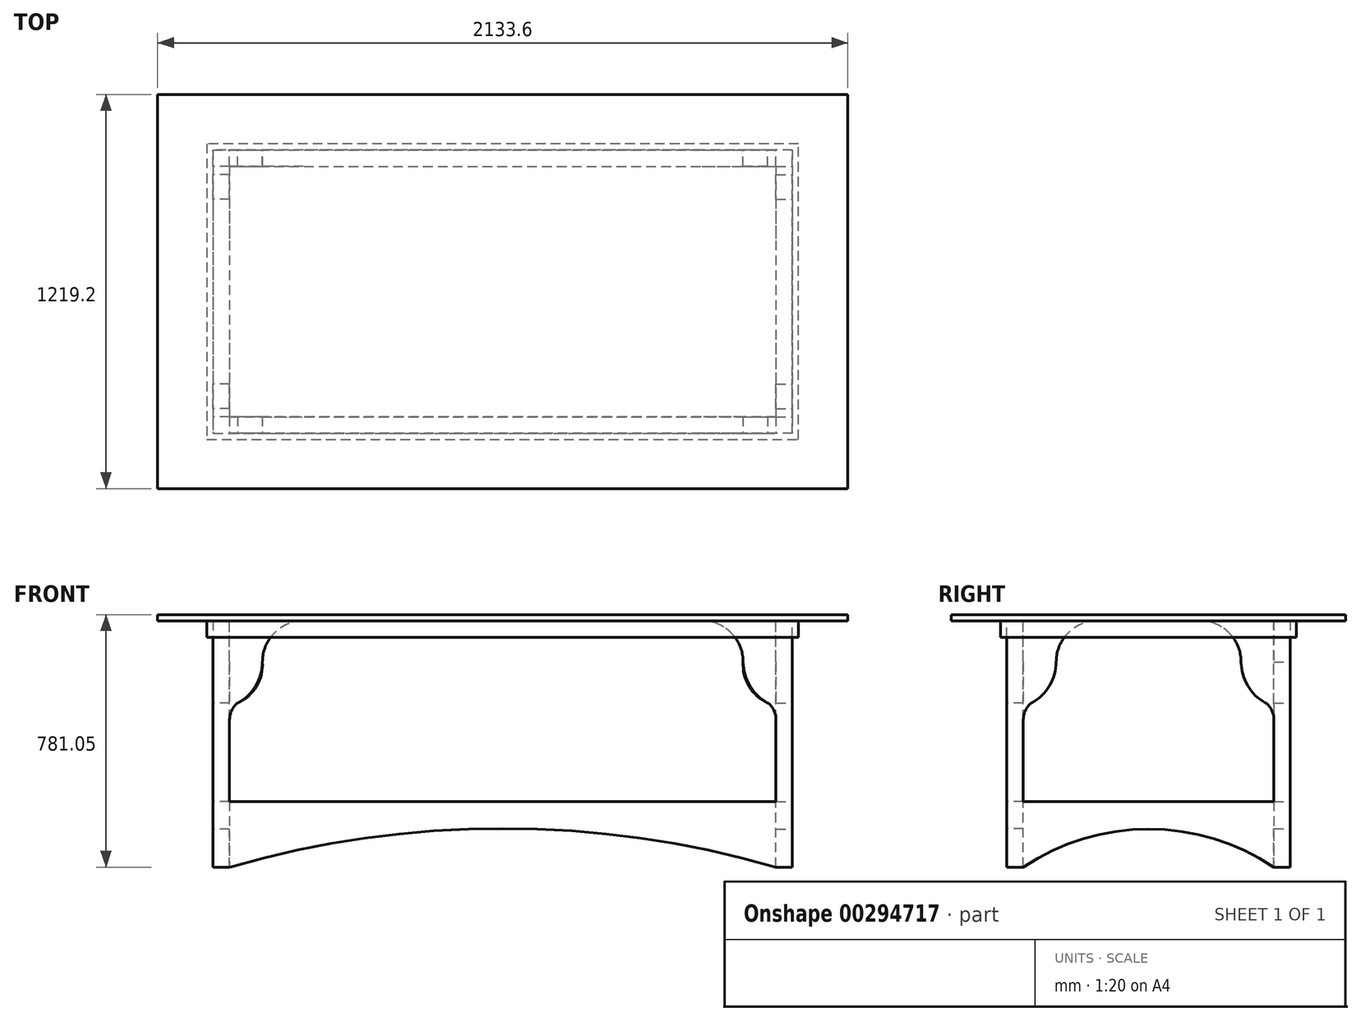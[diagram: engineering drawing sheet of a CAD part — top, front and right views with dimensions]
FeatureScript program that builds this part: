
annotation { "Feature Type Name" : "Feature", "Feature Type Description" : "" }
export const myFeature = defineFeature(function(context is Context, id is Id, definition is map)
    precondition{}
    {
        {
            var Q0;
            Q0=qCreatedBy(makeId("Top.planeOp"),FACE);
            var sketch = newSketch(context, id + "F0", { "sketchPlane" : qUnion([Q0])});
            skLineSegment(sketch, "E0", {"start": v(0, 609.6) * mm, "end": v(-1066.8, 609.6) * mm});
            skLineSegment(sketch, "E1", {"start": v(-1066.8, 609.6) * mm, "end": v(1066.8, 609.6) * mm});
            skLineSegment(sketch, "E2", {"start": v(1066.8, 609.6) * mm, "end": v(1066.8, -609.6) * mm});
            skLineSegment(sketch, "E3", {"start": v(1066.8, -609.6) * mm, "end": v(-1066.8, -609.6) * mm});
            skLineSegment(sketch, "E4", {"start": v(-1066.8, -609.6) * mm, "end": v(-1066.8, 609.6) * mm});
            skLineSegment(sketch, "E5", {"start": v(-1066.8, -609.6) * mm, "end": v(-1028.7, -609.6) * mm});
            skLineSegment(sketch, "E6", {"start": v(-1028.7, -571.5) * mm, "end": v(-1028.7, 571.5) * mm});
            skLineSegment(sketch, "E7", {"start": v(-1028.7, 571.5) * mm, "end": v(1028.7, 571.5) * mm});
            skLineSegment(sketch, "E8", {"start": v(1028.7, 571.5) * mm, "end": v(1028.7, -571.5) * mm});
            skLineSegment(sketch, "E9", {"start": v(1028.7, -571.5) * mm, "end": v(-1028.7, -571.5) * mm});
            skSolve(sketch);
        }
        {
            var Q0;
            Q0 = qSketchRegion(id + "F0", true);
            var Q1;
            Q1=makeQuery(id+"F0.imprint","IMPRINT",FACE,{"disambiguationData":[TD([[makeQuery(id+"F0.imprint","IMPRINT",EDGE,{"derivedFrom":sQuery(id+"F0.wireOp",EDGE,"E6")}),-1.0]])]});
            extrude(context, id + "F1", {"entities" : qUnion([Q0, Q1]), "depth" : 19.05 * mm});
        }
        {
            var Q0;
            Q0=makeQuery(id+"F1.opExtrude","CAP_FACE",FACE,{"disambiguationData":[OSD([sQuery(id+"F0.wireOp",EDGE,"E1"),sQuery(id+"F0.wireOp",EDGE,"E2"),sQuery(id+"F0.wireOp",EDGE,"E3"),sQuery(id+"F0.wireOp",EDGE,"E4"),sQuery(id+"F0.wireOp",EDGE,"E5")])],"isStart":true});
            var sketch = newSketch(context, id + "F2", { "sketchPlane" : qUnion([Q0])});
            skLineSegment(sketch, "E10", {"start": v(0, 0) * mm, "end": v(0, -457.2) * mm});
            skPoint(sketch, "E10.endSnap0", {"position": v(0, 609.6) * mm});
            skLineSegment(sketch, "E11", {"start": v(0, -457.2) * mm, "end": v(-914.4, -457.2) * mm});
            skLineSegment(sketch, "E12", {"start": v(-914.4, -457.2) * mm, "end": v(-914.4, 457.2) * mm});
            skLineSegment(sketch, "E13", {"start": v(-914.4, 457.2) * mm, "end": v(0, 457.2) * mm});
            skLineSegment(sketch, "E14", {"start": v(0, 457.2) * mm, "end": v(914.4, 457.2) * mm});
            skLineSegment(sketch, "E15", {"start": v(914.4, 457.2) * mm, "end": v(914.4, -457.2) * mm});
            skLineSegment(sketch, "E16", {"start": v(914.4, -457.2) * mm, "end": v(0, -457.2) * mm});
            skLineSegment(sketch, "E17.0", {"start": v(-895.35, -438.15) * mm, "end": v(-895.35, 438.15) * mm});
            skLineSegment(sketch, "E17.1", {"start": v(0, 438.15) * mm, "end": v(895.35, 438.15) * mm});
            skLineSegment(sketch, "E17.2", {"start": v(895.35, 438.15) * mm, "end": v(895.35, -438.15) * mm});
            skLineSegment(sketch, "E17.3", {"start": v(-895.35, 438.15) * mm, "end": v(0, 438.15) * mm});
            skLineSegment(sketch, "E17.4", {"start": v(895.35, -438.15) * mm, "end": v(0, -438.15) * mm});
            skLineSegment(sketch, "E17.5", {"start": v(0, -438.15) * mm, "end": v(-895.35, -438.15) * mm});
            skSolve(sketch);
        }
        {
            var Q0;
            Q0 = qSketchRegion(id + "F2", true);
            extrude(context, id + "F3", {"entities" : qUnion([Q0]), "operationType" : NewBodyOperationType.ADD, "depth" : 50.8 * mm});
        }
        {
            var Q0;
            Q0=makeQuery(id+"F3.opExtrude","SWEPT_FACE",FACE,{"disambiguationData":[OSD([sQuery(id+"F2.wireOp",EDGE,"E17.1"),sQuery(id+"F2.wireOp",EDGE,"E17.3")])]});
            var sketch = newSketch(context, id + "F4", { "sketchPlane" : qUnion([Q0])});
            skLineSegment(sketch, "E18", {"start": v(895.35, 0) * mm, "end": v(578.35, 0) * mm});
            skLineSegment(sketch, "E19", {"start": v(895.35, 0) * mm, "end": v(742.95, 0) * mm});
            skLineSegment(sketch, "E20", {"start": v(895.35, 0) * mm, "end": v(895.35, -762) * mm});
            skArc(sketch, "E21", {"start": v(742.95, -127) * mm, "mid": v(763.46, -201.05) * mm, "end": v(819.15, -254) * mm});
            skLineSegment(sketch, "E22", {"start": v(895.35, -762) * mm, "end": v(844.55, -762) * mm});
            skLineSegment(sketch, "E23", {"start": v(844.55, -762) * mm, "end": v(844.55, -304.8) * mm});
            skArc(sketch, "E24", {"start": v(844.55, -304.8) * mm, "mid": v(837.85, -276.4) * mm, "end": v(819.15, -254) * mm});
            skLineSegment(sketch, "E25", {"start": v(742.95, 0) * mm, "end": v(615.95, 0) * mm});
            skArc(sketch, "E26", {"start": v(742.95, -127) * mm, "mid": v(705.75, -37.2) * mm, "end": v(615.95, 0) * mm});
            skSolve(sketch);
        }
        {
            var Q0;
            Q0 = qSketchRegion(id + "F4", true);
            extrude(context, id + "F5", {"entities" : qUnion([Q0]), "operationType" : NewBodyOperationType.ADD, "depth" : 50.8 * mm});
        }
        {
            var Q0;
            Q0=makeQuery(id+"F3.opExtrude","SWEPT_FACE",FACE,{"disambiguationData":[OSD([sQuery(id+"F2.wireOp",EDGE,"E17.4"),sQuery(id+"F2.wireOp",EDGE,"E17.5")])]});
            var sketch = newSketch(context, id + "F6", { "sketchPlane" : qUnion([Q0])});
            skLineSegment(sketch, "E27", {"start": v(-895.35, 0) * mm, "end": v(-895.35, -762) * mm});
            skLineSegment(sketch, "E28", {"start": v(-895.35, -762) * mm, "end": v(-844.55, -762) * mm});
            skLineSegment(sketch, "E29", {"start": v(-844.55, -762) * mm, "end": v(-844.55, -304.8) * mm});
            skLineSegment(sketch, "E30", {"start": v(-895.35, 0) * mm, "end": v(-615.95, 0) * mm});
            skLineSegment(sketch, "E31", {"start": v(-615.95, 0) * mm, "end": v(-742.95, 0) * mm});
            skArc(sketch, "E32", {"start": v(-615.95, 0) * mm, "mid": v(-705.75, -37.2) * mm, "end": v(-742.95, -127) * mm});
            skLineSegment(sketch, "E33", {"start": v(-895.35, -127) * mm, "end": v(-895.35, -203.2) * mm});
            skArc(sketch, "E34", {"start": v(-819.15, -254) * mm, "mid": v(-760.9, -202.6) * mm, "end": v(-742.95, -127) * mm});
            skArc(sketch, "E35", {"start": v(-819.15, -254) * mm, "mid": v(-837.85, -276.4) * mm, "end": v(-844.55, -304.8) * mm});
            skSolve(sketch);
        }
        {
            var Q0;
            Q0 = qSketchRegion(id + "F6", true);
            extrude(context, id + "F7", {"entities" : qUnion([Q0]), "operationType" : NewBodyOperationType.ADD, "depth" : 50.8 * mm});
        }
        {
            var Q0;
            Q0=makeQuery(id+"F1.opExtrude","SWEPT_BODY",BODY,{"disambiguationData":[OSD([sQuery(id+"F0.wireOp",EDGE,"E1"),sQuery(id+"F0.wireOp",EDGE,"E2"),sQuery(id+"F0.wireOp",EDGE,"E3"),sQuery(id+"F0.wireOp",EDGE,"E4"),sQuery(id+"F0.wireOp",EDGE,"E5")])]});
            var Q1;
            Q1=qCreatedBy(makeId("Right.planeOp"),FACE);
            mirror(context, id + "F8", {"operationType" : NewBodyOperationType.ADD, "entities" : qUnion([Q0]), "mirrorPlane" : qUnion([Q1])});
        }
        {
            var Q0;
            Q0=makeQuery(id+"F8.opPattern","COPY",FACE,{"derivedFrom":makeQuery(id+"F5.opExtrude","CAP_FACE",FACE,{"disambiguationData":[OSD([sQuery(id+"F4.wireOp",EDGE,"E19"),sQuery(id+"F4.wireOp",EDGE,"E20"),sQuery(id+"F4.wireOp",EDGE,"E21"),sQuery(id+"F4.wireOp",EDGE,"E22"),sQuery(id+"F4.wireOp",EDGE,"E23"),sQuery(id+"F4.wireOp",EDGE,"E24"),sQuery(id+"F4.wireOp",EDGE,"E25"),sQuery(id+"F4.wireOp",EDGE,"E26")])],"isStart":true}),"instanceName":"1"});
            var sketch = newSketch(context, id + "F9", { "sketchPlane" : qUnion([Q0])});
            skLineSegment(sketch, "E36", {"start": v(-844.55, -762) * mm, "end": v(-844.55, -558.8) * mm});
            skLineSegment(sketch, "E37", {"start": v(-844.55, -558.8) * mm, "end": v(844.55, -558.8) * mm});
            skLineSegment(sketch, "E38", {"start": v(844.55, -558.8) * mm, "end": v(844.55, -762) * mm});
            skArc(sketch, "E39", {"start": v(844.55, -762) * mm, "mid": v(0, -642.66) * mm, "end": v(-844.55, -762) * mm});
            skSolve(sketch);
        }
        {
            var Q0;
            Q0 = qSketchRegion(id + "F9", true);
            extrude(context, id + "F10", {"entities" : qUnion([Q0]), "operationType" : NewBodyOperationType.ADD, "oppositeDirection" : true, "depth" : 50.8 * mm});
        }
        {
            var Q0;
            Q0=makeQuery(id+"F7.opExtrude","CAP_FACE",FACE,{"disambiguationData":[OSD([sQuery(id+"F6.wireOp",EDGE,"E27"),sQuery(id+"F6.wireOp",EDGE,"E28"),sQuery(id+"F6.wireOp",EDGE,"E29"),sQuery(id+"F6.wireOp",EDGE,"E30"),sQuery(id+"F6.wireOp",EDGE,"E31"),sQuery(id+"F6.wireOp",EDGE,"E32"),sQuery(id+"F6.wireOp",EDGE,"E33"),sQuery(id+"F6.wireOp",EDGE,"E34"),sQuery(id+"F6.wireOp",EDGE,"E35")])],"isStart":true});
            var sketch = newSketch(context, id + "F11", { "sketchPlane" : qUnion([Q0])});
            skLineSegment(sketch, "E40", {"start": v(844.55, -762) * mm, "end": v(844.55, -558.8) * mm});
            skLineSegment(sketch, "E41", {"start": v(844.55, -558.8) * mm, "end": v(-844.55, -558.8) * mm});
            skLineSegment(sketch, "E42", {"start": v(-844.55, -558.8) * mm, "end": v(-844.55, -762) * mm});
            skArc(sketch, "E43", {"start": v(844.55, -762) * mm, "mid": v(0, -642.66) * mm, "end": v(-844.55, -762) * mm});
            skSolve(sketch);
        }
        {
            var Q0;
            Q0 = qSketchRegion(id + "F11", true);
            extrude(context, id + "F12", {"entities" : qUnion([Q0]), "operationType" : NewBodyOperationType.ADD, "oppositeDirection" : true, "depth" : 50.8 * mm});
        }
        {
            var Q0;
            Q0=makeQuery(id+"F3.opExtrude","SWEPT_FACE",FACE,{"disambiguationData":[OSD([sQuery(id+"F2.wireOp",EDGE,"E17.0")])]});
            var sketch = newSketch(context, id + "F13", { "sketchPlane" : qUnion([Q0])});
            skLineSegment(sketch, "E44", {"start": v(-387.35, -762) * mm, "end": v(-387.35, -560.28) * mm});
            skLineSegment(sketch, "E45", {"start": v(-387.35, -560.28) * mm, "end": v(387.35, -560.28) * mm});
            skLineSegment(sketch, "E46", {"start": v(387.35, -560.28) * mm, "end": v(387.35, -762) * mm});
            skPoint(sketch, "E47.endSnap0", {"position": v(0, -762) * mm});
            skArc(sketch, "E48", {"start": v(387.35, -762) * mm, "mid": v(0, -644.14) * mm, "end": v(-387.35, -762) * mm});
            skSolve(sketch);
        }
        {
            var Q0;
            Q0 = qSketchRegion(id + "F13", true);
            extrude(context, id + "F14", {"entities" : qUnion([Q0]), "operationType" : NewBodyOperationType.ADD, "depth" : 50.8 * mm});
        }
        {
            var Q0;
            Q0=makeQuery(id+"F3.opExtrude","SWEPT_FACE",FACE,{"disambiguationData":[OSD([sQuery(id+"F2.wireOp",EDGE,"E17.2")])]});
            var sketch = newSketch(context, id + "F15", { "sketchPlane" : qUnion([Q0])});
            skLineSegment(sketch, "E49", {"start": v(-387.35, -762) * mm, "end": v(-387.35, -558.8) * mm});
            skLineSegment(sketch, "E50", {"start": v(-387.35, -558.8) * mm, "end": v(387.35, -558.8) * mm});
            skArc(sketch, "E51", {"start": v(387.35, -762) * mm, "mid": v(0, -642.66) * mm, "end": v(-387.35, -762) * mm});
            skLineSegment(sketch, "E52", {"start": v(387.35, -762) * mm, "end": v(387.35, -558.8) * mm});
            skSolve(sketch);
        }
        {
            var Q0;
            Q0 = qSketchRegion(id + "F15", true);
            extrude(context, id + "F16", {"entities" : qUnion([Q0]), "operationType" : NewBodyOperationType.ADD, "depth" : 50.8 * mm});
        }
        {
            var Q0;
            Q0=makeQuery(id+"F3.opExtrude","SWEPT_FACE",FACE,{"disambiguationData":[OSD([sQuery(id+"F2.wireOp",EDGE,"E17.0")])]});
            var sketch = newSketch(context, id + "F17", { "sketchPlane" : qUnion([Q0])});
            skLineSegment(sketch, "E53", {"start": v(438.15, 0) * mm, "end": v(158.75, 0) * mm});
            skArc(sketch, "E54", {"start": v(285.75, -127) * mm, "mid": v(248.55, -37.2) * mm, "end": v(158.75, 0) * mm});
            skArc(sketch, "E55", {"start": v(285.75, -127) * mm, "mid": v(306.26, -201.05) * mm, "end": v(361.95, -254) * mm});
            skArc(sketch, "E56", {"start": v(387.35, -304.8) * mm, "mid": v(380.65, -276.4) * mm, "end": v(361.95, -254) * mm});
            skLineSegment(sketch, "E57", {"start": v(387.35, -304.8) * mm, "end": v(387.35, 0) * mm});
            skPoint(sketch, "E58.endSnap0", {"position": v(0, 0) * mm});
            skArc(sketch, "E59.MirrorCS", {"start": v(-387.35, -304.8) * mm, "mid": v(-380.65, -276.4) * mm, "end": v(-361.95, -254) * mm});
            skLineSegment(sketch, "E60.MirrorCS", {"start": v(-438.15, 0) * mm, "end": v(-158.75, 0) * mm});
            skArc(sketch, "E61.MirrorCS", {"start": v(-285.75, -127) * mm, "mid": v(-306.26, -201.05) * mm, "end": v(-361.95, -254) * mm});
            skLineSegment(sketch, "E62.MirrorCS", {"start": v(-387.35, -304.8) * mm, "end": v(-387.35, 0) * mm});
            skArc(sketch, "E63.MirrorCS", {"start": v(-285.75, -127) * mm, "mid": v(-248.55, -37.2) * mm, "end": v(-158.75, 0) * mm});
            skSolve(sketch);
        }
        {
            var Q0;
            Q0 = qSketchRegion(id + "F17", true);
            extrude(context, id + "F18", {"entities" : qUnion([Q0]), "operationType" : NewBodyOperationType.ADD, "depth" : 50.8 * mm});
        }
        {
            var Q0;
            Q0=makeQuery(id+"F1.opExtrude","SWEPT_BODY",BODY,{"disambiguationData":[OSD([sQuery(id+"F0.wireOp",EDGE,"E1"),sQuery(id+"F0.wireOp",EDGE,"E2"),sQuery(id+"F0.wireOp",EDGE,"E3"),sQuery(id+"F0.wireOp",EDGE,"E4"),sQuery(id+"F0.wireOp",EDGE,"E5")])]});
            var Q1;
            Q1=qCreatedBy(makeId("Right.planeOp"),FACE);
            mirror(context, id + "F19", {"operationType" : NewBodyOperationType.ADD, "entities" : qUnion([Q0]), "mirrorPlane" : qUnion([Q1])});
        }
    });
